# Revit family: PRE050007-FR
name_source: partatom
category: Accessoire de canalisation
revit_build: Autodesk Revit 2017 (Build: 20160225_1515(x64)
units: mm (PartAtom-declared; Revit-internal decimal feet)

## family parameters
Basée sur le plan de construction = Non
Cote de connecteur circulaire = Utiliser le diamètre
Couper avec des vides une fois chargée = Non
Partagée = Non
Toujours verticalement = Oui
Type d'élément = Normal

## types (1)
- 68232 PRESTO MITIGEUR TEMPORISE 7000 MANETTE+FLEXIBLES PEX
    Adresse = 7, RUE RACINE - 92542 MONTROUGE CEDEX FRANCE
    Debit = 3 l/min à 3 bars, réglage 4 positions

Dispositif anti-coup de bélier
    Description = Mitigeur bi-commande temporisé sur plage, à manette omnidirectionnelle et sélecteur de température latéral. De type Presto 7000 réf. 68232 ou techniquement équivalent. Avec mécanisme à rubis auto nettoyé par fil frein, débit préréglé à 3 l/mn. Réglage de débit interne. Avec flexibles PEX, robinets d’arrêt et filtres.
    Diamètre Nominal = 12 mm  [stored 0.0393701 ft]
    Fabricant = LES ROBINETS PRESTO S.A.
    Finition = Corps en laiton avec finition chromée
    Flux = 0.1 L/s
    Fonction = Pression d'utilisation recommandée :
- 1 à 5 bars

Débit :
- 3 l/mn à 3 bars - Réglage 4 positions
- Dispositif anti-coup de bélier

Durée d'écoulement :
- 15 secondes ± 5 secondes

Fonctionnement :
- Par simple action sur la manette omnidirectionnelle (déclenchement
  souple)

Alimentation hydraulique :
- G 3/8'' (12x17)

Résistance thermique :
- Ce robinet résiste à une température de 75°C durant 30 minutes dans
  le cadre de chocs thermiques

Sécurité :
- Repère par point de couleur inusable et indémontable (bleu ou rouge)

Livré avec :
- 2 Robinets d'arrêt MM G 3/8'' (12x17)
- 2 Joints filtre
- 1 Rondelle de serrage inox
- 2 Flexibles PEX avec clapets anti-retour NF et écrous tournants
- 1 Bride de fixation
- 1 Joint de bride
- 1 Ecrou de fixation
- 2 Pions, bleu et rouge

Normes / Agréments :
- Corps en laiton chromé conforme aux normes NF EN1982 / NF EN12164 /
  NF EN12165
- Traitement de surface Nickel-Chrome selon NF EN12540
- Résistance au brouillard salin neutre (NSS) : 200 h selon NF ISO 9227
    Garantie = 10
    Hauteur = 172 mm  [stored 0.564304 ft]
    LC = 28 mm
    Largeur = 75 mm  [stored 0.246063 ft]
    Lien CCTP = http://www.prestodatashare.com
    Lien fiche produit = http://www.prestodatashare.com
    Lien notice d'utilisation = http://www.prestodatashare.com
    Matériau = Laiton poli chromé
    Modèle = 68232 PRESTO MITIGEUR TEMPORISE 7000 MANETTE+FLEXIBLES PEX
    PC = 23 mm
    Perte de charge = 0.0 Pa
    Polantis code = PRE050007-FR
    Pression = 1 à 5 bars
    Profondeur = 152 mm  [stored 0.498688 ft]
    Raccordement = G 3/8'' (12x17)
    Reference = 68232
    URL = http://www.prestodatashare.com
    URL Fabricant = http://www.prestodatashare.com
    Variantes = 68232

note: [stored X ft] marks values corroborated as IEEE doubles in the binary element streams (Revit-internal decimal feet)
